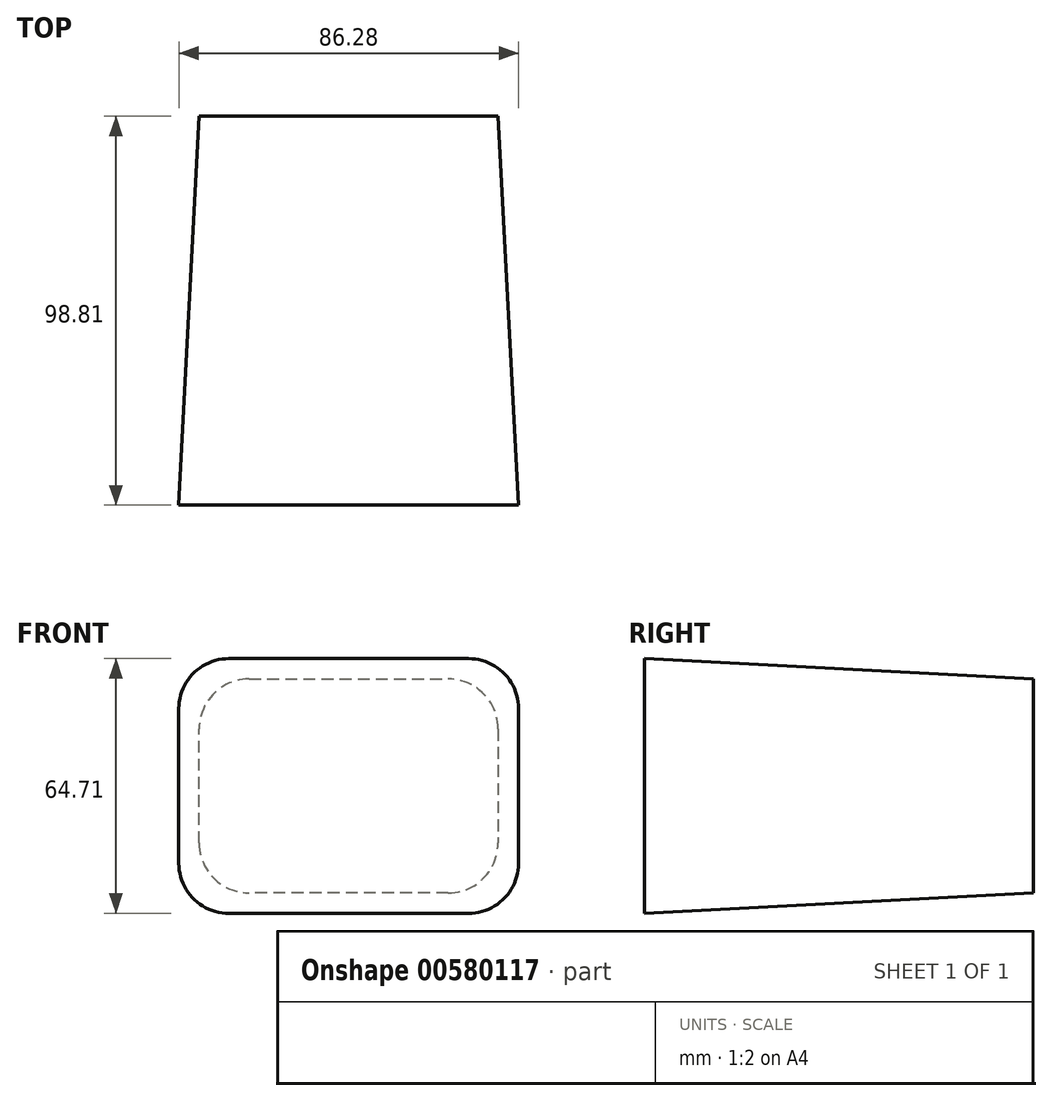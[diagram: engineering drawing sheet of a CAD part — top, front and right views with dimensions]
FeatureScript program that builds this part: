
annotation { "Feature Type Name" : "Feature", "Feature Type Description" : "" }
export const myFeature = defineFeature(function(context is Context, id is Id, definition is map)
    precondition{}
    {
        {
            var Q0;
            Q0=qCreatedBy(makeId("Front.planeOp"),FACE);
            var sketch = newSketch(context, id + "F0", { "sketchPlane" : qUnion([Q0])});
            skLineSegment(sketch, "E0.bottom", {"start": v(37.13, -17.63) * mm, "end": v(-38.8, -17.63) * mm});
            skLineSegment(sketch, "E0.top", {"start": v(37.13, 36.72) * mm, "end": v(-38.8, 36.72) * mm});
            skLineSegment(sketch, "E0.left", {"start": v(37.13, -17.63) * mm, "end": v(37.13, 36.72) * mm});
            skLineSegment(sketch, "E0.right", {"start": v(-38.8, -17.63) * mm, "end": v(-38.8, 36.72) * mm});
            skSolve(sketch);
        }
        {
            var Q0;
            Q0=makeQuery(id+"F0.imprint","IMPRINT",FACE,{"disambiguationData":[TD([[makeQuery(id+"F0.imprint","IMPRINT",EDGE,{"derivedFrom":sQuery(id+"F0.wireOp",EDGE,"E0.bottom")}),-1.0]])]});
            extrude(context, id + "F1", {"entities" : qUnion([Q0]), "depth" : 98.8 * mm, "offsetDistance" : 25.4 * mm, "hasDraft" : true, "draftAngle" : 3 * degree});
        }
        {
            var Q0;
            Q0=makeQuery(id+"F1.opExtrude","SWEPT_EDGE",EDGE,{"disambiguationData":[OSD([sQuery(id+"F0.wireOp",EDGE,"E0.top"),sQuery(id+"F0.wireOp",EDGE,"E0.left")])]});
            var Q1;
            Q1=makeQuery(id+"F1.opExtrude","SWEPT_EDGE",EDGE,{"disambiguationData":[OSD([sQuery(id+"F0.wireOp",EDGE,"E0.top"),sQuery(id+"F0.wireOp",EDGE,"E0.right")])]});
            var Q2;
            Q2=makeQuery(id+"F1.opExtrude","SWEPT_EDGE",EDGE,{"disambiguationData":[OSD([sQuery(id+"F0.wireOp",EDGE,"E0.bottom"),sQuery(id+"F0.wireOp",EDGE,"E0.left")])]});
            var Q3;
            Q3=makeQuery(id+"F1.opExtrude","SWEPT_EDGE",EDGE,{"disambiguationData":[OSD([sQuery(id+"F0.wireOp",EDGE,"E0.bottom"),sQuery(id+"F0.wireOp",EDGE,"E0.right")])]});
            fillet(context, id + "F2", {"entities" : qUnion([Q0, Q1, Q2, Q3]), "radius" : 12.7 * mm, "tangentPropagation" : true, "allowEdgeOverflow" : false});
        }
    });
